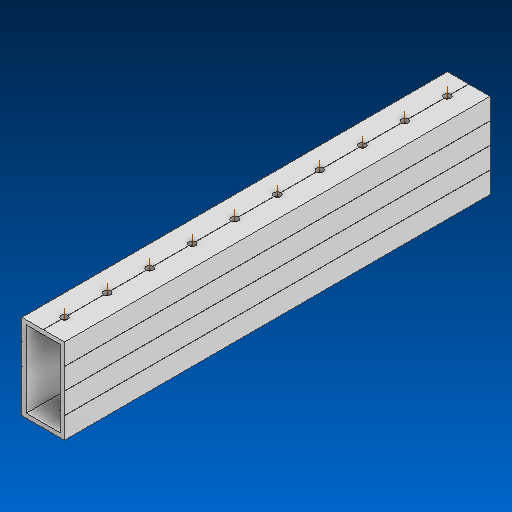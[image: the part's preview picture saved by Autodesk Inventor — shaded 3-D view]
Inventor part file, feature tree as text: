
AUTODESK INVENTOR PART (.ipt)
format: ipt  version: 2022.2 (Build 262287000, 287)  size: 467,456 bytes
history: native  units: in
note: dims shown in document units (in); Inventor stores cm internally (conversion verified against a paired STEP export)
features: other x11, extrude x1, pattern_linear x1, sketch x1
ambient origin geometry x8: Origin, YZ Plane, XZ Plane, XY Plane, X Axis, Y Axis, Z Axis, Center Point
bodies: Solid1 (feature_tree)
feature tree (14):
  extrude  "Extrusion1"  Depth=2.0in
  other  "Work Axis1"
  pattern_linear  "Rectangular Pattern1"  Spacing1=49.0in  [1 undecoded]
  sketch  "Sketch1"  dims[d0=1.0in d1=2.0in d2=49.0in d3=0.0in d4=3.937in d6=1.0in]
  other  "Work Axis2"
  other  "Work Axis3"
  other  "Work Axis4"
  other  "Work Axis5"
  other  "Work Axis6"
  other  "Work Axis7"
  other  "Work Axis8"
  other  "Work Axis9"
  other  "Work Axis10"
  other  "Cut-Extrude2"
note: 1 required parameter value undecoded (feature->parameter linkage not recoverable at this tier; creation-order binding heuristic only, values carry confidence <= 0.55)
